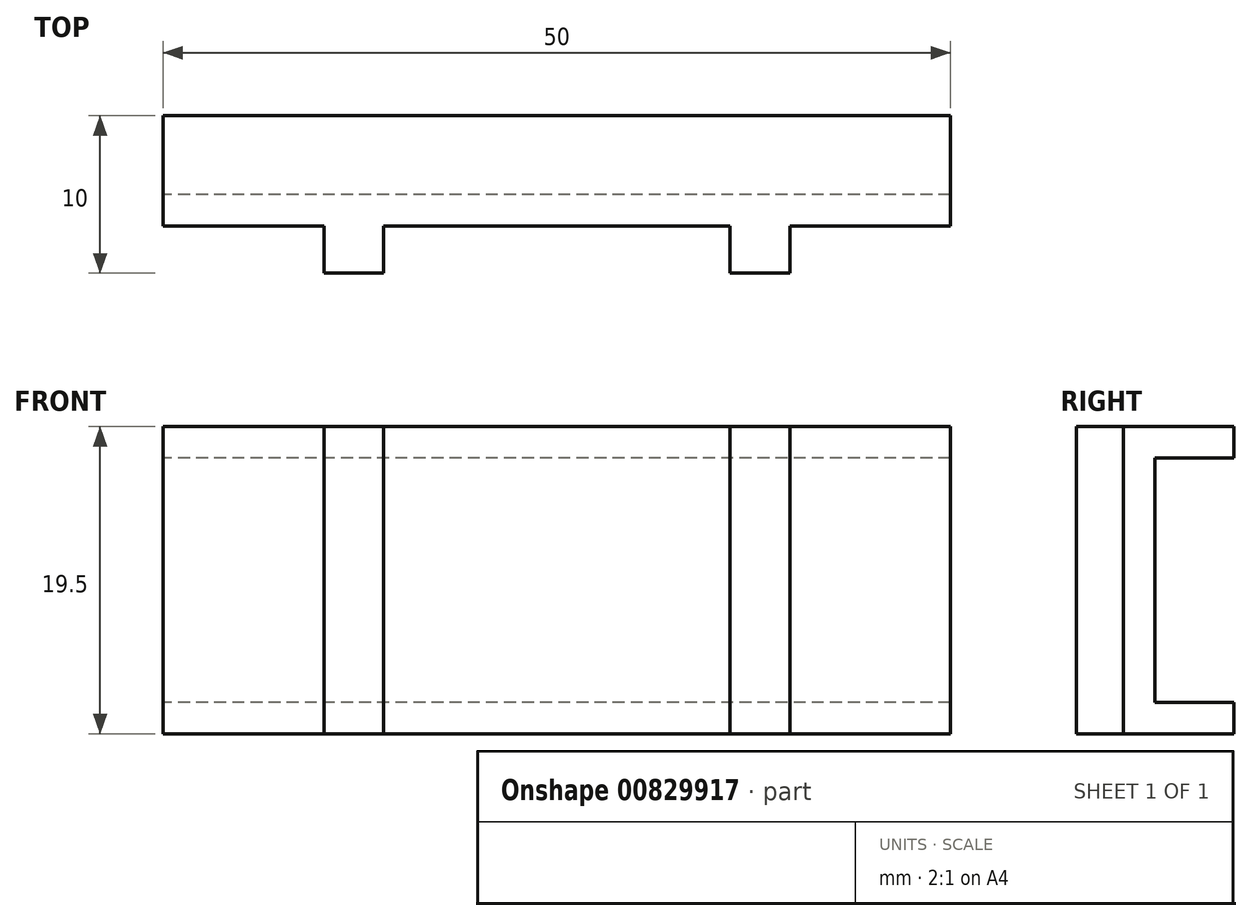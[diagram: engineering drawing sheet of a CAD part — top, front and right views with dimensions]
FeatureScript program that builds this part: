
annotation { "Feature Type Name" : "Feature", "Feature Type Description" : "" }
export const myFeature = defineFeature(function(context is Context, id is Id, definition is map)
    precondition{}
    {
        {
            var Q0;
            Q0=qCreatedBy(makeId("Front.planeOp"),FACE);
            var sketch = newSketch(context, id + "F0", { "sketchPlane" : qUnion([Q0])});
            skLineSegment(sketch, "E0.bottom", {"start": v(25, -9.75) * mm, "end": v(-25, -9.75) * mm});
            skLineSegment(sketch, "E0.top", {"start": v(25, 9.75) * mm, "end": v(-25, 9.75) * mm});
            skLineSegment(sketch, "E0.left", {"start": v(25, -9.75) * mm, "end": v(25, 9.75) * mm});
            skLineSegment(sketch, "E0.right", {"start": v(-25, -9.75) * mm, "end": v(-25, 9.75) * mm});
            skPoint(sketch, "E0.middle", {"position": v(0, 0) * mm});
            skSolve(sketch);
        }
        {
            var Q0;
            Q0 = qSketchRegion(id + "F0", true);
            extrude(context, id + "F1", {"entities" : qUnion([Q0]), "depth" : 15 * mm, "offsetDistance" : 25 * mm});
        }
        {
            var Q0;
            Q0=makeQuery(id+"F1.opExtrude","CAP_FACE",FACE,{"disambiguationData":[OSD([sQuery(id+"F0.wireOp",EDGE,"E0.bottom"),sQuery(id+"F0.wireOp",EDGE,"E0.top"),sQuery(id+"F0.wireOp",EDGE,"E0.left"),sQuery(id+"F0.wireOp",EDGE,"E0.right")])],"isStart":true});
            var sketch = newSketch(context, id + "F2", { "sketchPlane" : qUnion([Q0])});
            skLineSegment(sketch, "E1.bottom", {"start": v(-25, 7.75) * mm, "end": v(25, 7.75) * mm});
            skLineSegment(sketch, "E1.top", {"start": v(-25, -7.75) * mm, "end": v(25, -7.75) * mm});
            skLineSegment(sketch, "E1.left", {"start": v(-25, 7.75) * mm, "end": v(-25, -7.75) * mm});
            skLineSegment(sketch, "E1.right", {"start": v(25, 7.75) * mm, "end": v(25, -7.75) * mm});
            skPoint(sketch, "E1.middle", {"position": v(0, 0) * mm});
            skSolve(sketch);
        }
        {
            var Q0;
            Q0=makeQuery(id+"F2.imprint","IMPRINT",FACE,{"disambiguationData":[TD([[makeQuery(id+"F2.imprint","IMPRINT",EDGE,{"derivedFrom":sQuery(id+"F2.wireOp",EDGE,"E1.bottom")}),-1.0]])]});
            extrude(context, id + "F3", {"entities" : qUnion([Q0]), "operationType" : NewBodyOperationType.REMOVE, "oppositeDirection" : true, "depth" : 10 * mm, "offsetDistance" : 25 * mm});
        }
        {
            var Q0;
            Q0=makeQuery(id+"F1.opExtrude","CAP_FACE",FACE,{"disambiguationData":[OSD([sQuery(id+"F0.wireOp",EDGE,"E0.bottom"),sQuery(id+"F0.wireOp",EDGE,"E0.top"),sQuery(id+"F0.wireOp",EDGE,"E0.left"),sQuery(id+"F0.wireOp",EDGE,"E0.right")])],"isStart":false});
            var sketch = newSketch(context, id + "F4", { "sketchPlane" : qUnion([Q0])});
            skLineSegment(sketch, "E2.bottom", {"start": v(-11, 9.75) * mm, "end": v(11, 9.75) * mm});
            skLineSegment(sketch, "E2.top", {"start": v(-11, -9.75) * mm, "end": v(11, -9.75) * mm});
            skLineSegment(sketch, "E2.left", {"start": v(-11, 9.75) * mm, "end": v(-11, -9.75) * mm});
            skLineSegment(sketch, "E2.right", {"start": v(11, 9.75) * mm, "end": v(11, -9.75) * mm});
            skPoint(sketch, "E2.middle", {"position": v(0, 0) * mm});
            skSolve(sketch);
        }
        {
            var Q0;
            Q0 = qSketchRegion(id + "F4", true);
            extrude(context, id + "F5", {"entities" : qUnion([Q0]), "operationType" : NewBodyOperationType.REMOVE, "oppositeDirection" : true, "depth" : 3 * mm, "offsetDistance" : 25 * mm});
        }
        {
            var Q0;
            {var subQ0=sQuery(id+"F0.wireOp",EDGE,"E0.bottom");var subQ1=sQuery(id+"F0.wireOp",EDGE,"E0.top");var subQ2=sQuery(id+"F0.wireOp",EDGE,"E0.left");Q0=makeQuery(id+"F5.boolean.opBoolean","SPLIT",FACE,{"disambiguationData":[TD([makeQuery(id+"F1.opExtrude","SWEPT_FACE",FACE,{"disambiguationData":[OSD([subQ2])]})])],"derivedFrom":makeQuery(id+"F1.opExtrude","CAP_FACE",FACE,{"disambiguationData":[OSD([subQ0,subQ1,subQ2,sQuery(id+"F0.wireOp",EDGE,"E0.right")])],"isStart":false})});}
            var sketch = newSketch(context, id + "F6", { "sketchPlane" : qUnion([Q0])});
            skLineSegment(sketch, "E3.bottom", {"start": v(11, -9.75) * mm, "end": v(14.8, -9.75) * mm});
            skLineSegment(sketch, "E3.top", {"start": v(11, 9.75) * mm, "end": v(14.8, 9.75) * mm});
            skLineSegment(sketch, "E3.left", {"start": v(11, -9.75) * mm, "end": v(11, 9.75) * mm});
            skLineSegment(sketch, "E3.right", {"start": v(14.8, -9.75) * mm, "end": v(14.8, 9.75) * mm});
            skPoint(sketch, "E4", {"position": v(-10.98, -9.76) * mm});
            skLineSegment(sketch, "E5.bottom", {"start": v(-10.98, -9.76) * mm, "end": v(-14.78, -9.76) * mm});
            skLineSegment(sketch, "E5.top", {"start": v(-10.98, 9.74) * mm, "end": v(-14.78, 9.74) * mm});
            skLineSegment(sketch, "E5.left", {"start": v(-10.98, -9.76) * mm, "end": v(-10.98, 9.74) * mm});
            skLineSegment(sketch, "E5.right", {"start": v(-14.78, -9.76) * mm, "end": v(-14.78, 9.74) * mm});
            skLineSegment(sketch, "E6.bottom", {"start": v(-14.78, -9.76) * mm, "end": v(-25, -9.76) * mm});
            skLineSegment(sketch, "E6.top", {"start": v(-14.78, 9.74) * mm, "end": v(-25, 9.74) * mm});
            skLineSegment(sketch, "E6.right", {"start": v(-25, -9.76) * mm, "end": v(-25, 9.74) * mm});
            skSolve(sketch);
        }
        {
            var Q0;
            {var subQ0=sQuery(id+"F6.wireOp",EDGE,"E3.right");Q0=makeQuery(id+"F6.imprint","IMPRINT",FACE,{"disambiguationData":[TD([[makeQuery(id+"F6.imprint","IMPRINT",EDGE,{"derivedFrom":subQ0}),-1.0]])]});}
            var Q1;
            Q1=makeQuery(id+"F6.imprint","IMPRINT",FACE,{"disambiguationData":[TD([[makeQuery(id+"F6.imprint","IMPRINT",EDGE,{"derivedFrom":sQuery(id+"F6.wireOp",EDGE,"E6.bottom")}),-1.0]])]});
            extrude(context, id + "F7", {"entities" : qUnion([Q0, Q1]), "operationType" : NewBodyOperationType.REMOVE, "oppositeDirection" : true, "depth" : 3 * mm, "offsetDistance" : 25 * mm});
        }
        {
            var Q0;
            {var subQ0=sQuery(id+"F0.wireOp",EDGE,"E0.top");var subQ1=sQuery(id+"F0.wireOp",EDGE,"E0.left");var subQ2=sQuery(id+"F0.wireOp",EDGE,"E0.right");Q0=makeQuery(id+"F3.boolean.opBoolean","SPLIT",FACE,{"disambiguationData":[TD([makeQuery(id+"F1.opExtrude","SWEPT_FACE",FACE,{"disambiguationData":[OSD([subQ0])]})])],"derivedFrom":makeQuery(id+"F1.opExtrude","CAP_FACE",FACE,{"disambiguationData":[OSD([sQuery(id+"F0.wireOp",EDGE,"E0.bottom"),subQ0,subQ1,subQ2])],"isStart":true})});}
            var Q1;
            {var subQ0=sQuery(id+"F0.wireOp",EDGE,"E0.bottom");var subQ1=sQuery(id+"F0.wireOp",EDGE,"E0.right");var subQ2=sQuery(id+"F0.wireOp",EDGE,"E0.left");Q1=makeQuery(id+"F3.boolean.opBoolean","SPLIT",FACE,{"disambiguationData":[TD([makeQuery(id+"F1.opExtrude","SWEPT_FACE",FACE,{"disambiguationData":[OSD([subQ0])]})])],"derivedFrom":makeQuery(id+"F1.opExtrude","CAP_FACE",FACE,{"disambiguationData":[OSD([subQ0,sQuery(id+"F0.wireOp",EDGE,"E0.top"),subQ2,subQ1])],"isStart":true})});}
            extrude(context, id + "F8", {"entities" : qUnion([Q0, Q1]), "operationType" : NewBodyOperationType.REMOVE, "oppositeDirection" : true, "depth" : 5 * mm, "offsetDistance" : 25 * mm});
        }
    });
